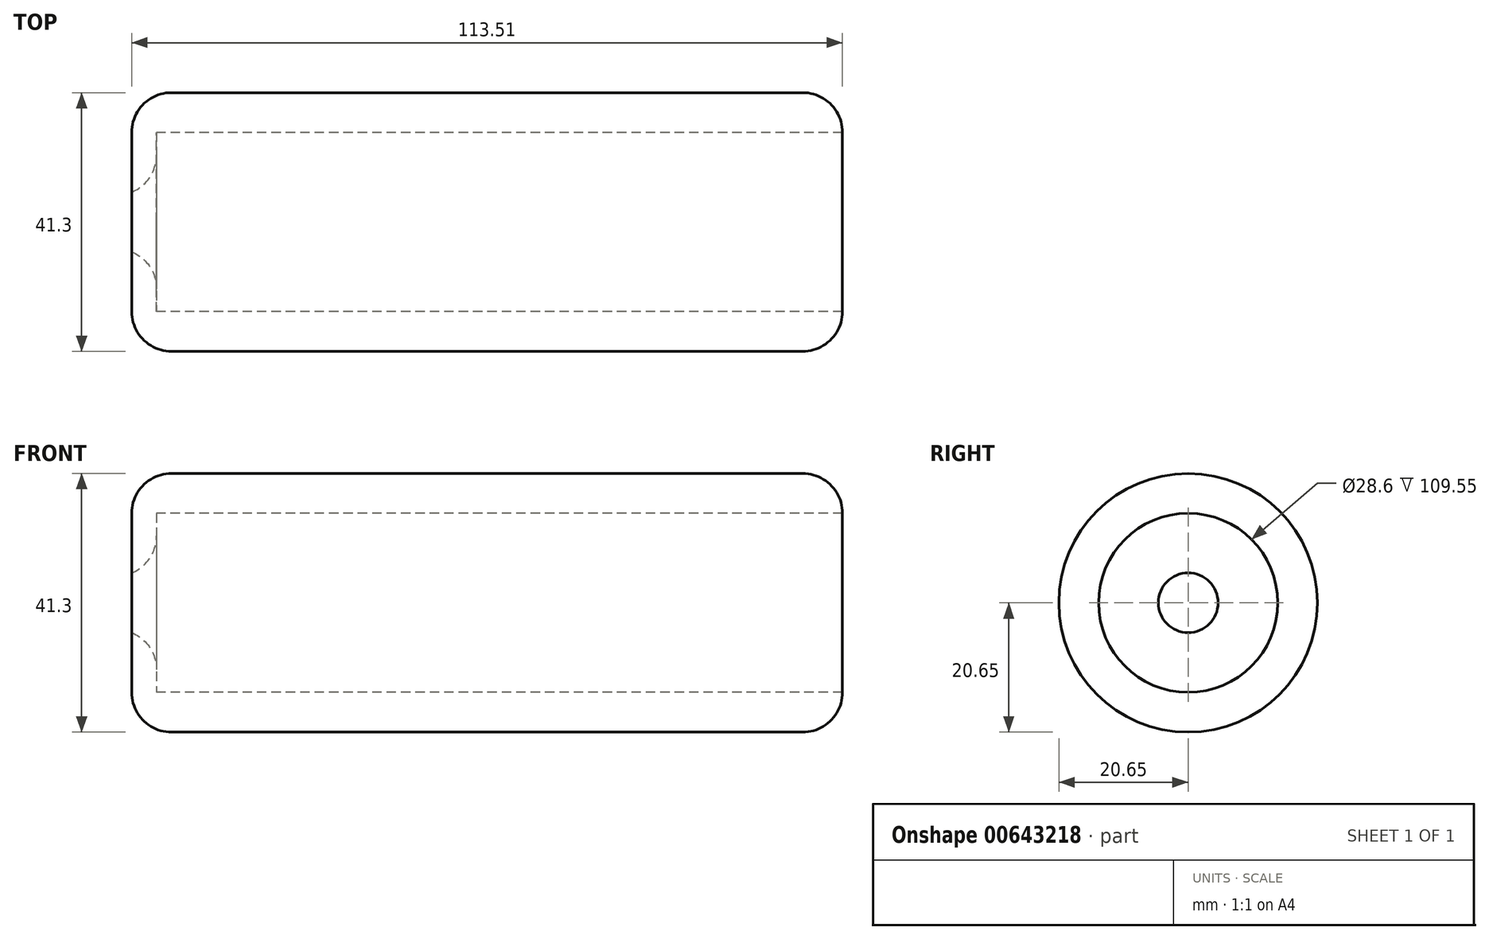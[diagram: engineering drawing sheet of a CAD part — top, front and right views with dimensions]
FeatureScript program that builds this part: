
annotation { "Feature Type Name" : "Feature", "Feature Type Description" : "" }
export const myFeature = defineFeature(function(context is Context, id is Id, definition is map)
    precondition{}
    {
        {
            var Q0;
            Q0=qCreatedBy(makeId("Front.planeOp"),FACE);
            var sketch = newSketch(context, id + "F0", { "sketchPlane" : qUnion([Q0])});
            skLineSegment(sketch, "E0", {"start": v(-75.23, 0) * mm, "end": v(38.28, 0) * mm});
            skLineSegment(sketch, "E1", {"start": v(38.28, 0) * mm, "end": v(38.28, 6.35) * mm});
            skLineSegment(sketch, "E2", {"start": v(38.28, 6.35) * mm, "end": v(-71.02, 6.35) * mm});
            skLineSegment(sketch, "E3", {"start": v(-75.23, 0) * mm, "end": v(-75.23, 15.88) * mm});
            skLineSegment(sketch, "E4", {"start": v(-75.23, 15.88) * mm, "end": v(-71.27, 15.88) * mm});
            skLineSegment(sketch, "E5", {"start": v(-71.27, 15.88) * mm, "end": v(-71.27, 6.35) * mm});
            skLineSegment(sketch, "E6", {"start": v(-71.27, 6.35) * mm, "end": v(-71.02, 6.35) * mm});
            skLineSegment(sketch, "E7", {"start": v(-75.23, 20.65) * mm, "end": v(40.9, 20.65) * mm, "construction": true});
            skLineSegment(sketch, "E8", {"start": v(-75.23, 20.65) * mm, "end": v(-75.23, 15.88) * mm, "construction": true});
            skSolve(sketch);
        }
        {
            var Q0;
            Q0=makeQuery(id+"F0.imprint","IMPRINT",FACE,{"disambiguationData":[TD([[makeQuery(id+"F0.imprint","IMPRINT",EDGE,{"derivedFrom":sQuery(id+"F0.wireOp",EDGE,"E0")}),1.0]])]});
            var Q1;
            Q1=sQuery(id+"F0.wireOp",EDGE,"E7");
            revolve(context, id + "F1", {"entities" : qUnion([Q0]), "axis" : qUnion([Q1]), "revolveType" : RevolveType.FULL});
        }
        {
            var Q0;
            Q0=makeQuery(id+"F1.opRevolve","SWEPT_EDGE",EDGE,{"disambiguationData":[OSD([sQuery(id+"F0.wireOp",EDGE,"E0"),sQuery(id+"F0.wireOp",EDGE,"E1")])]});
            var Q1;
            Q1=makeQuery(id+"F1.opRevolve","SWEPT_EDGE",EDGE,{"disambiguationData":[OSD([sQuery(id+"F0.wireOp",EDGE,"E4"),sQuery(id+"F0.wireOp",EDGE,"E5")])]});
            fillet(context, id + "F2", {"entities" : qUnion([Q0, Q1]), "radius" : 6.35 * mm, "tangentPropagation" : true, "allowEdgeOverflow" : false});
        }
        {
            var Q0;
            Q0=makeQuery(id+"F1.opRevolve","SWEPT_EDGE",EDGE,{"disambiguationData":[OSD([sQuery(id+"F0.wireOp",EDGE,"E0"),sQuery(id+"F0.wireOp",EDGE,"E3")])]});
            fillet(context, id + "F3", {"entities" : qUnion([Q0]), "radius" : 6.35 * mm, "tangentPropagation" : true, "allowEdgeOverflow" : false});
        }
    });
